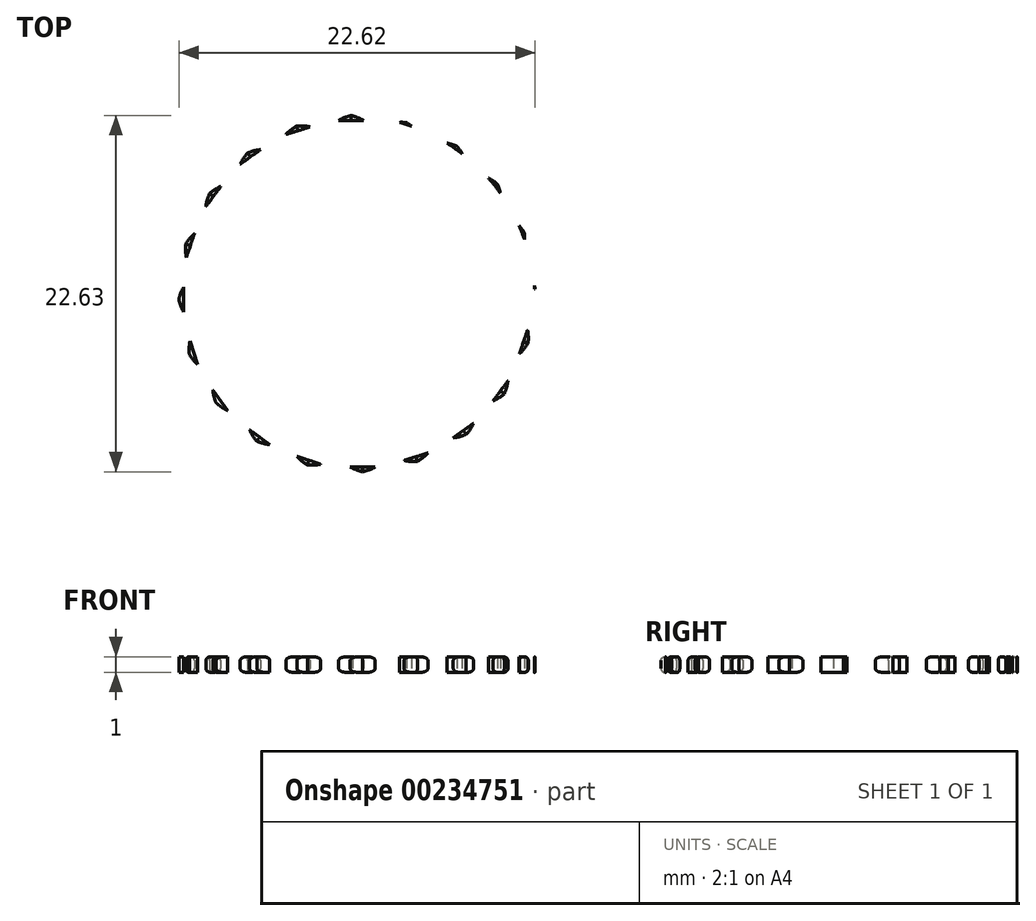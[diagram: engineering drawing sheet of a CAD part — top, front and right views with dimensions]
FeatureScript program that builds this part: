
annotation { "Feature Type Name" : "Feature", "Feature Type Description" : "" }
export const myFeature = defineFeature(function(context is Context, id is Id, definition is map)
    precondition{}
    {
        {
            assignVariable(context, id + "F0", {"name" : "GearDepth", "anyValue" : 1});
        }
        {
            assignVariable(context, id + "F1", {"name" : "TeethFillet", "anyValue" : getVariable(context, 'GearDepth') * .25});
        }
        {
            var Q0;
            Q0=qCreatedBy(makeId("Top.planeOp"),FACE);
            var sketch = newSketch(context, id + "F2", { "sketchPlane" : qUnion([Q0])});
            skCircle(sketch, "E0", {"center": v(0, 0) * mm, "radius": 11.8 * mm});
            skCircle(sketch, "E1", {"center": v(0, 0) * mm, "radius": 11.65 * mm, "construction": true});
            skCircle(sketch, "E2", {"center": v(0, 0) * mm, "radius": 11.5 * mm, "construction": true});
            skLineSegment(sketch, "E3", {"start": v(0, 0) * mm, "end": v(0, 17.6) * mm, "construction": true});
            skLineSegment(sketch, "E4", {"start": v(0, 0) * mm, "end": v(0.18, 18.05) * mm, "construction": true});
            skLineSegment(sketch, "E5", {"start": v(0, 11.65) * mm, "end": v(-10.54, 11.65) * mm, "construction": true});
            skLineSegment(sketch, "E6", {"start": v(0, 11.65) * mm, "end": v(-10.3, 7.9) * mm, "construction": true});
            skCircle(sketch, "E7", {"center": v(0, 11.65) * mm, "radius": 2.91 * mm, "construction": true});
            skCircle(sketch, "E8", {"center": v(-2.74, 10.65) * mm, "radius": 2.91 * mm, "construction": true});
            skArc(sketch, "E9", {"start": v(-5.47, 11.65) * mm, "mid": v(-5.64, 10.86) * mm, "end": v(-5.59, 10.05) * mm});
            skArc(sketch, "E10.trimOffspring", {"start": v(0.2, 11.79) * mm, "mid": v(-0.26, 11.67) * mm, "end": v(-0.68, 11.48) * mm});
            skArc(sketch, "E11.MirrorCS", {"start": v(0.04, 11.8) * mm, "mid": v(0.49, 11.67) * mm, "end": v(0.9, 11.46) * mm});
            skLineSegment(sketch, "E12", {"start": v(-0.68, 11.48) * mm, "end": v(0.9, 11.46) * mm});
            skArc(sketch, "E13.1.0", {"start": v(-3.3, 11.15) * mm, "mid": v(-3.69, 10.9) * mm, "end": v(-4.03, 10.58) * mm});
            skLineSegment(sketch, "E13.1.1", {"start": v(-4.03, 10.58) * mm, "end": v(-2.51, 11.06) * mm});
            skArc(sketch, "E13.1.2", {"start": v(-3.44, 11.1) * mm, "mid": v(-2.97, 11.12) * mm, "end": v(-2.51, 11.06) * mm});
            skArc(sketch, "E13.2.0", {"start": v(-6.4, 9.46) * mm, "mid": v(-6.7, 9.1) * mm, "end": v(-6.93, 8.7) * mm});
            skLineSegment(sketch, "E13.2.1", {"start": v(-6.93, 8.7) * mm, "end": v(-5.64, 9.62) * mm});
            skArc(sketch, "E13.2.2", {"start": v(-6.53, 9.37) * mm, "mid": v(-6.1, 9.53) * mm, "end": v(-5.64, 9.62) * mm});
            skArc(sketch, "E13.3.0", {"start": v(-8.85, 6.9) * mm, "mid": v(-9.02, 6.46) * mm, "end": v(-9.11, 6) * mm});
            skLineSegment(sketch, "E13.3.1", {"start": v(-9.11, 6) * mm, "end": v(-8.17, 7.28) * mm});
            skArc(sketch, "E13.3.2", {"start": v(-8.94, 6.77) * mm, "mid": v(-8.58, 7.06) * mm, "end": v(-8.17, 7.28) * mm});
            skArc(sketch, "E13.4.0", {"start": v(-10.38, 3.7) * mm, "mid": v(-10.4, 3.23) * mm, "end": v(-10.35, 2.77) * mm});
            skLineSegment(sketch, "E13.4.1", {"start": v(-10.35, 2.77) * mm, "end": v(-9.85, 4.27) * mm});
            skArc(sketch, "E13.4.2", {"start": v(-10.43, 3.55) * mm, "mid": v(-10.17, 3.94) * mm, "end": v(-9.85, 4.27) * mm});
            skArc(sketch, "E13.5.0", {"start": v(-10.85, 0.18) * mm, "mid": v(-10.73, -0.27) * mm, "end": v(-10.54, -0.7) * mm});
            skLineSegment(sketch, "E13.5.1", {"start": v(-10.54, -0.7) * mm, "end": v(-10.52, 0.9) * mm});
            skArc(sketch, "E13.5.2", {"start": v(-10.85, 0.03) * mm, "mid": v(-10.72, 0.48) * mm, "end": v(-10.52, 0.9) * mm});
            skArc(sketch, "E13.6.0", {"start": v(-10.2, -3.3) * mm, "mid": v(-9.95, -3.7) * mm, "end": v(-9.64, -4.04) * mm});
            skLineSegment(sketch, "E13.6.1", {"start": v(-9.64, -4.04) * mm, "end": v(-10.11, -2.52) * mm});
            skArc(sketch, "E13.6.2", {"start": v(-10.16, -3.45) * mm, "mid": v(-10.18, -2.98) * mm, "end": v(-10.11, -2.52) * mm});
            skArc(sketch, "E13.7.0", {"start": v(-8.52, -6.42) * mm, "mid": v(-8.16, -6.71) * mm, "end": v(-7.75, -6.94) * mm});
            skLineSegment(sketch, "E13.7.1", {"start": v(-7.75, -6.94) * mm, "end": v(-8.67, -5.65) * mm});
            skArc(sketch, "E13.7.2", {"start": v(-8.43, -6.54) * mm, "mid": v(-8.59, -6.1) * mm, "end": v(-8.67, -5.65) * mm});
            skArc(sketch, "E13.8.0", {"start": v(-5.95, -8.86) * mm, "mid": v(-5.52, -9.03) * mm, "end": v(-5.06, -9.12) * mm});
            skLineSegment(sketch, "E13.8.1", {"start": v(-5.06, -9.12) * mm, "end": v(-6.34, -8.18) * mm});
            skArc(sketch, "E13.8.2", {"start": v(-5.83, -8.95) * mm, "mid": v(-6.11, -8.59) * mm, "end": v(-6.34, -8.18) * mm});
            skArc(sketch, "E13.9.0", {"start": v(-2.75, -10.39) * mm, "mid": v(-2.29, -10.42) * mm, "end": v(-1.82, -10.36) * mm});
            skLineSegment(sketch, "E13.9.1", {"start": v(-1.82, -10.36) * mm, "end": v(-3.33, -9.86) * mm});
            skArc(sketch, "E13.9.2", {"start": v(-2.6, -10.44) * mm, "mid": v(-3, -10.18) * mm, "end": v(-3.33, -9.86) * mm});
            skArc(sketch, "E13.10.0", {"start": v(0.76, -10.85) * mm, "mid": v(1.21, -10.74) * mm, "end": v(1.64, -10.54) * mm});
            skLineSegment(sketch, "E13.10.1", {"start": v(1.64, -10.54) * mm, "end": v(0.05, -10.53) * mm});
            skArc(sketch, "E13.10.2", {"start": v(0.91, -10.86) * mm, "mid": v(0.47, -10.73) * mm, "end": v(0.05, -10.53) * mm});
            skArc(sketch, "E13.11.0", {"start": v(4.25, -10.21) * mm, "mid": v(4.64, -9.96) * mm, "end": v(4.98, -9.65) * mm});
            skLineSegment(sketch, "E13.11.1", {"start": v(4.98, -9.65) * mm, "end": v(3.47, -10.12) * mm});
            skArc(sketch, "E13.11.2", {"start": v(4.4, -10.17) * mm, "mid": v(3.93, -10.19) * mm, "end": v(3.47, -10.12) * mm});
            skArc(sketch, "E13.12.0", {"start": v(7.36, -8.52) * mm, "mid": v(7.66, -8.17) * mm, "end": v(7.89, -7.76) * mm});
            skLineSegment(sketch, "E13.12.1", {"start": v(7.89, -7.76) * mm, "end": v(6.6, -8.68) * mm});
            skArc(sketch, "E13.12.2", {"start": v(7.49, -8.44) * mm, "mid": v(7.05, -8.6) * mm, "end": v(6.6, -8.68) * mm});
            skArc(sketch, "E13.13.0", {"start": v(9.8, -5.96) * mm, "mid": v(9.98, -5.52) * mm, "end": v(10.07, -5.07) * mm});
            skLineSegment(sketch, "E13.13.1", {"start": v(10.07, -5.07) * mm, "end": v(9.12, -6.34) * mm});
            skArc(sketch, "E13.13.2", {"start": v(9.9, -5.83) * mm, "mid": v(9.53, -6.12) * mm, "end": v(9.12, -6.34) * mm});
            skArc(sketch, "E13.14.0", {"start": v(11.33, -2.76) * mm, "mid": v(11.36, -2.3) * mm, "end": v(11.3, -1.83) * mm});
            skLineSegment(sketch, "E13.14.1", {"start": v(11.3, -1.83) * mm, "end": v(10.8, -3.34) * mm});
            skArc(sketch, "E13.14.2", {"start": v(11.38, -2.62) * mm, "mid": v(11.12, -3) * mm, "end": v(10.8, -3.34) * mm});
            skArc(sketch, "E13.15.0", {"start": v(11.8, 0.75) * mm, "mid": v(11.68, 1.2) * mm, "end": v(11.49, 1.63) * mm});
            skLineSegment(sketch, "E13.15.1", {"start": v(11.49, 1.63) * mm, "end": v(11.47, 0.04) * mm});
            skArc(sketch, "E13.15.2", {"start": v(11.8, 0.9) * mm, "mid": v(11.68, 0.46) * mm, "end": v(11.47, 0.04) * mm});
            skArc(sketch, "E13.16.0", {"start": v(11.16, 4.24) * mm, "mid": v(10.9, 4.63) * mm, "end": v(10.6, 4.97) * mm});
            skLineSegment(sketch, "E13.16.1", {"start": v(10.6, 4.97) * mm, "end": v(11.07, 3.46) * mm});
            skArc(sketch, "E13.16.2", {"start": v(11.11, 4.38) * mm, "mid": v(11.13, 3.92) * mm, "end": v(11.07, 3.46) * mm});
            skArc(sketch, "E13.17.0", {"start": v(9.47, 7.35) * mm, "mid": v(9.11, 7.65) * mm, "end": v(8.7, 7.88) * mm});
            skLineSegment(sketch, "E13.17.1", {"start": v(8.7, 7.88) * mm, "end": v(9.63, 6.58) * mm});
            skArc(sketch, "E13.17.2", {"start": v(9.38, 7.48) * mm, "mid": v(9.54, 7.04) * mm, "end": v(9.63, 6.58) * mm});
            skArc(sketch, "E13.18.0", {"start": v(6.9, 9.8) * mm, "mid": v(6.47, 9.97) * mm, "end": v(6.01, 10.06) * mm});
            skLineSegment(sketch, "E13.18.1", {"start": v(6.01, 10.06) * mm, "end": v(7.29, 9.11) * mm});
            skArc(sketch, "E13.18.2", {"start": v(6.78, 9.89) * mm, "mid": v(7.07, 9.52) * mm, "end": v(7.29, 9.11) * mm});
            skArc(sketch, "E13.19.0", {"start": v(3.7, 11.32) * mm, "mid": v(3.24, 11.35) * mm, "end": v(2.78, 11.3) * mm});
            skLineSegment(sketch, "E13.19.1", {"start": v(2.78, 11.3) * mm, "end": v(4.28, 10.8) * mm});
            skArc(sketch, "E13.19.2", {"start": v(3.56, 11.37) * mm, "mid": v(3.95, 11.11) * mm, "end": v(4.28, 10.8) * mm});
            skPoint(sketch, "E13.center", {"position": v(0.48, 0.47) * mm});
            skCircle(sketch, "E14", {"center": v(0, 0) * mm, "radius": 2.5 * mm});
            skSolve(sketch);
        }
        {
            var Q0;
            {var subQ0=sQuery(id+"F2.wireOp",EDGE,"E10.trimOffspring");Q0=makeQuery(id+"F2.imprint","IMPRINT",FACE,{"disambiguationData":[TD([[makeQuery(id+"F2.imprint","IMPRINT",EDGE,{"derivedFrom":subQ0}),1.0]])]});}
            var Q1;
            {var subQ0=sQuery(id+"F2.wireOp",EDGE,"E0");var subQ1=makeQuery(id+"F2.imprint","INTERSECT",VERTEX,{"derivedFrom":[subQ0,sQuery(id+"F2.wireOp",EDGE,"E10.trimOffspring")]});Q1=makeQuery(id+"F2.imprint","IMPRINT",FACE,{"disambiguationData":[TD([[makeQuery(id+"F2.imprint","IMPRINT",EDGE,{"disambiguationData":[TD([[subQ1,-1.0]])],"derivedFrom":subQ0}),1.0]])]});}
            var Q2;
            {var subQ0=sQuery(id+"F2.wireOp",EDGE,"E13.1.0");Q2=makeQuery(id+"F2.imprint","IMPRINT",FACE,{"disambiguationData":[TD([[makeQuery(id+"F2.imprint","IMPRINT",EDGE,{"derivedFrom":subQ0}),1.0]])]});}
            var Q3;
            {var subQ0=sQuery(id+"F2.wireOp",EDGE,"E13.2.0");Q3=makeQuery(id+"F2.imprint","IMPRINT",FACE,{"disambiguationData":[TD([[makeQuery(id+"F2.imprint","IMPRINT",EDGE,{"derivedFrom":subQ0}),1.0]])]});}
            var Q4;
            {var subQ0=sQuery(id+"F2.wireOp",EDGE,"E13.3.0");Q4=makeQuery(id+"F2.imprint","IMPRINT",FACE,{"disambiguationData":[TD([[makeQuery(id+"F2.imprint","IMPRINT",EDGE,{"derivedFrom":subQ0}),1.0]])]});}
            var Q5;
            {var subQ0=sQuery(id+"F2.wireOp",EDGE,"E13.4.0");Q5=makeQuery(id+"F2.imprint","IMPRINT",FACE,{"disambiguationData":[TD([[makeQuery(id+"F2.imprint","IMPRINT",EDGE,{"derivedFrom":subQ0}),1.0]])]});}
            var Q6;
            {var subQ0=sQuery(id+"F2.wireOp",EDGE,"E13.5.0");Q6=makeQuery(id+"F2.imprint","IMPRINT",FACE,{"disambiguationData":[TD([[makeQuery(id+"F2.imprint","IMPRINT",EDGE,{"derivedFrom":subQ0}),1.0]])]});}
            var Q7;
            {var subQ0=sQuery(id+"F2.wireOp",EDGE,"E13.6.0");Q7=makeQuery(id+"F2.imprint","IMPRINT",FACE,{"disambiguationData":[TD([[makeQuery(id+"F2.imprint","IMPRINT",EDGE,{"derivedFrom":subQ0}),1.0]])]});}
            var Q8;
            {var subQ0=sQuery(id+"F2.wireOp",EDGE,"E13.7.0");Q8=makeQuery(id+"F2.imprint","IMPRINT",FACE,{"disambiguationData":[TD([[makeQuery(id+"F2.imprint","IMPRINT",EDGE,{"derivedFrom":subQ0}),1.0]])]});}
            var Q9;
            {var subQ0=sQuery(id+"F2.wireOp",EDGE,"E13.8.0");Q9=makeQuery(id+"F2.imprint","IMPRINT",FACE,{"disambiguationData":[TD([[makeQuery(id+"F2.imprint","IMPRINT",EDGE,{"derivedFrom":subQ0}),1.0]])]});}
            var Q10;
            {var subQ0=sQuery(id+"F2.wireOp",EDGE,"E13.9.0");Q10=makeQuery(id+"F2.imprint","IMPRINT",FACE,{"disambiguationData":[TD([[makeQuery(id+"F2.imprint","IMPRINT",EDGE,{"derivedFrom":subQ0}),1.0]])]});}
            var Q11;
            {var subQ0=sQuery(id+"F2.wireOp",EDGE,"E13.10.0");Q11=makeQuery(id+"F2.imprint","IMPRINT",FACE,{"disambiguationData":[TD([[makeQuery(id+"F2.imprint","IMPRINT",EDGE,{"derivedFrom":subQ0}),1.0]])]});}
            var Q12;
            {var subQ0=sQuery(id+"F2.wireOp",EDGE,"E13.11.0");Q12=makeQuery(id+"F2.imprint","IMPRINT",FACE,{"disambiguationData":[TD([[makeQuery(id+"F2.imprint","IMPRINT",EDGE,{"derivedFrom":subQ0}),1.0]])]});}
            var Q13;
            {var subQ0=sQuery(id+"F2.wireOp",EDGE,"E13.12.0");Q13=makeQuery(id+"F2.imprint","IMPRINT",FACE,{"disambiguationData":[TD([[makeQuery(id+"F2.imprint","IMPRINT",EDGE,{"derivedFrom":subQ0}),1.0]])]});}
            var Q14;
            {var subQ0=sQuery(id+"F2.wireOp",EDGE,"E13.13.0");Q14=makeQuery(id+"F2.imprint","IMPRINT",FACE,{"disambiguationData":[TD([[makeQuery(id+"F2.imprint","IMPRINT",EDGE,{"derivedFrom":subQ0}),1.0]])]});}
            var Q15;
            {var subQ0=sQuery(id+"F2.wireOp",EDGE,"E13.14.0");Q15=makeQuery(id+"F2.imprint","IMPRINT",FACE,{"disambiguationData":[TD([[makeQuery(id+"F2.imprint","IMPRINT",EDGE,{"derivedFrom":subQ0}),1.0]])]});}
            var Q16;
            {var subQ0=sQuery(id+"F2.wireOp",EDGE,"E13.15.0");Q16=makeQuery(id+"F2.imprint","IMPRINT",FACE,{"disambiguationData":[TD([[makeQuery(id+"F2.imprint","IMPRINT",EDGE,{"derivedFrom":subQ0}),1.0]])]});}
            var Q17;
            {var subQ0=sQuery(id+"F2.wireOp",EDGE,"E13.16.0");Q17=makeQuery(id+"F2.imprint","IMPRINT",FACE,{"disambiguationData":[TD([[makeQuery(id+"F2.imprint","IMPRINT",EDGE,{"derivedFrom":subQ0}),1.0]])]});}
            var Q18;
            {var subQ0=sQuery(id+"F2.wireOp",EDGE,"E13.17.0");Q18=makeQuery(id+"F2.imprint","IMPRINT",FACE,{"disambiguationData":[TD([[makeQuery(id+"F2.imprint","IMPRINT",EDGE,{"derivedFrom":subQ0}),1.0]])]});}
            var Q19;
            {var subQ0=sQuery(id+"F2.wireOp",EDGE,"E13.18.0");Q19=makeQuery(id+"F2.imprint","IMPRINT",FACE,{"disambiguationData":[TD([[makeQuery(id+"F2.imprint","IMPRINT",EDGE,{"derivedFrom":subQ0}),1.0]])]});}
            var Q20;
            {var subQ0=sQuery(id+"F2.wireOp",EDGE,"E13.19.0");Q20=makeQuery(id+"F2.imprint","IMPRINT",FACE,{"disambiguationData":[TD([[makeQuery(id+"F2.imprint","IMPRINT",EDGE,{"derivedFrom":subQ0}),1.0]])]});}
            var Q21;
            Q21=sQuery(id+"F2.wireOp",EDGE,"E0");
            var Q22;
            Q22=sQuery(id+"F2.wireOp",EDGE,"E10.trimOffspring");
            var Q23;
            Q23=sQuery(id+"F2.wireOp",EDGE,"E12");
            var Q24;
            Q24=sQuery(id+"F2.wireOp",EDGE,"E11.MirrorCS");
            extrude(context, id + "F3", {"entities" : qUnion([Q0, Q1, Q2, Q3, Q4, Q5, Q6, Q7, Q8, Q9, Q10, Q11, Q12, Q13, Q14, Q15, Q16, Q17, Q18, Q19, Q20]), "surfaceEntities" : qUnion([Q21, Q22, Q23, Q24]), "depth" : (getVariable(context, 'GearDepth')) * mm});
        }
        {
            var Q0;
            Q0=makeQuery(id+"F3.opExtrude","CAP_EDGE",EDGE,{"disambiguationData":[OSD([sQuery(id+"F2.wireOp",EDGE,"E13.5.2")])],"isStart":false});
            var Q1;
            Q1=makeQuery(id+"F3.opExtrude","CAP_EDGE",EDGE,{"disambiguationData":[OSD([sQuery(id+"F2.wireOp",EDGE,"E13.5.1")])],"isStart":false});
            var Q2;
            {var subQ0=sQuery(id+"F2.wireOp",EDGE,"E0");Q2=makeQuery(id+"F3.opExtrude","CAP_EDGE",EDGE,{"disambiguationData":[OSD([subQ0]),TDD([makeQuery(id+"F2.imprint","IMPRINT",EDGE,{"disambiguationData":[TD([[makeQuery(id+"F2.imprint","INTERSECT",VERTEX,{"derivedFrom":[subQ0,sQuery(id+"F2.wireOp",EDGE,"E13.5.2")]}),-1.0]])],"derivedFrom":subQ0})])],"isStart":false});}
            var Q3;
            Q3=makeQuery(id+"F3.opExtrude","CAP_EDGE",EDGE,{"disambiguationData":[OSD([sQuery(id+"F2.wireOp",EDGE,"E13.6.0")])],"isStart":false});
            var Q4;
            Q4=makeQuery(id+"F3.opExtrude","CAP_EDGE",EDGE,{"disambiguationData":[OSD([sQuery(id+"F2.wireOp",EDGE,"E13.6.1")])],"isStart":false});
            var Q5;
            Q5=makeQuery(id+"F3.opExtrude","CAP_EDGE",EDGE,{"disambiguationData":[OSD([sQuery(id+"F2.wireOp",EDGE,"E13.6.2")])],"isStart":false});
            var Q6;
            {var subQ0=sQuery(id+"F2.wireOp",EDGE,"E0");Q6=makeQuery(id+"F3.opExtrude","SWEPT_FACE",FACE,{"disambiguationData":[OSD([subQ0]),TDD([makeQuery(id+"F2.imprint","IMPRINT",EDGE,{"disambiguationData":[TD([[makeQuery(id+"F2.imprint","INTERSECT",VERTEX,{"derivedFrom":[subQ0,sQuery(id+"F2.wireOp",EDGE,"E13.6.2")]}),-1.0]])],"derivedFrom":subQ0})])]});}
            var Q7;
            {var subQ0=sQuery(id+"F2.wireOp",EDGE,"E0");Q7=makeQuery(id+"F3.opExtrude","CAP_EDGE",EDGE,{"disambiguationData":[OSD([subQ0]),TDD([makeQuery(id+"F2.imprint","IMPRINT",EDGE,{"disambiguationData":[TD([[makeQuery(id+"F2.imprint","INTERSECT",VERTEX,{"derivedFrom":[subQ0,sQuery(id+"F2.wireOp",EDGE,"E13.6.2")]}),-1.0]])],"derivedFrom":subQ0})])],"isStart":false});}
            var Q8;
            Q8=makeQuery(id+"F3.opExtrude","CAP_EDGE",EDGE,{"disambiguationData":[OSD([sQuery(id+"F2.wireOp",EDGE,"E13.7.2")])],"isStart":true});
            var Q9;
            {var subQ0=sQuery(id+"F2.wireOp",EDGE,"E0");Q9=makeQuery(id+"F3.opExtrude","CAP_EDGE",EDGE,{"disambiguationData":[OSD([subQ0]),TDD([makeQuery(id+"F2.imprint","IMPRINT",EDGE,{"disambiguationData":[TD([[makeQuery(id+"F2.imprint","INTERSECT",VERTEX,{"derivedFrom":[subQ0,sQuery(id+"F2.wireOp",EDGE,"E13.7.2")]}),-1.0]])],"derivedFrom":subQ0})])],"isStart":true});}
            var Q10;
            Q10=makeQuery(id+"F3.opExtrude","CAP_EDGE",EDGE,{"disambiguationData":[OSD([sQuery(id+"F2.wireOp",EDGE,"E13.7.2")])],"isStart":false});
            var Q11;
            {var subQ0=sQuery(id+"F2.wireOp",EDGE,"E0");Q11=makeQuery(id+"F3.opExtrude","CAP_EDGE",EDGE,{"disambiguationData":[OSD([subQ0]),TDD([makeQuery(id+"F2.imprint","IMPRINT",EDGE,{"disambiguationData":[TD([[makeQuery(id+"F2.imprint","INTERSECT",VERTEX,{"derivedFrom":[subQ0,sQuery(id+"F2.wireOp",EDGE,"E13.7.2")]}),-1.0]])],"derivedFrom":subQ0})])],"isStart":false});}
            var Q12;
            Q12=makeQuery(id+"F3.opExtrude","CAP_EDGE",EDGE,{"disambiguationData":[OSD([sQuery(id+"F2.wireOp",EDGE,"E13.8.0")])],"isStart":false});
            var Q13;
            {var subQ0=sQuery(id+"F2.wireOp",EDGE,"E0");Q13=makeQuery(id+"F3.opExtrude","SWEPT_FACE",FACE,{"disambiguationData":[OSD([subQ0]),TDD([makeQuery(id+"F2.imprint","IMPRINT",EDGE,{"disambiguationData":[TD([[makeQuery(id+"F2.imprint","INTERSECT",VERTEX,{"derivedFrom":[subQ0,sQuery(id+"F2.wireOp",EDGE,"E13.7.2")]}),-1.0]])],"derivedFrom":subQ0})])]});}
            var Q14;
            Q14=makeQuery(id+"F3.opExtrude","CAP_EDGE",EDGE,{"disambiguationData":[OSD([sQuery(id+"F2.wireOp",EDGE,"E13.6.0")])],"isStart":true});
            var Q15;
            Q15=makeQuery(id+"F3.opExtrude","CAP_EDGE",EDGE,{"disambiguationData":[OSD([sQuery(id+"F2.wireOp",EDGE,"E13.8.2")])],"isStart":false});
            var Q16;
            {var subQ0=sQuery(id+"F2.wireOp",EDGE,"E0");Q16=makeQuery(id+"F3.opExtrude","CAP_EDGE",EDGE,{"disambiguationData":[OSD([subQ0]),TDD([makeQuery(id+"F2.imprint","IMPRINT",EDGE,{"disambiguationData":[TD([[makeQuery(id+"F2.imprint","INTERSECT",VERTEX,{"derivedFrom":[subQ0,sQuery(id+"F2.wireOp",EDGE,"E13.8.2")]}),-1.0]])],"derivedFrom":subQ0})])],"isStart":false});}
            var Q17;
            Q17=makeQuery(id+"F3.opExtrude","CAP_EDGE",EDGE,{"disambiguationData":[OSD([sQuery(id+"F2.wireOp",EDGE,"E13.9.0")])],"isStart":false});
            var Q18;
            Q18=makeQuery(id+"F3.opExtrude","CAP_EDGE",EDGE,{"disambiguationData":[OSD([sQuery(id+"F2.wireOp",EDGE,"E13.9.2")])],"isStart":false});
            var Q19;
            {var subQ0=sQuery(id+"F2.wireOp",EDGE,"E0");Q19=makeQuery(id+"F3.opExtrude","CAP_EDGE",EDGE,{"disambiguationData":[OSD([subQ0]),TDD([makeQuery(id+"F2.imprint","IMPRINT",EDGE,{"disambiguationData":[TD([[makeQuery(id+"F2.imprint","INTERSECT",VERTEX,{"derivedFrom":[subQ0,sQuery(id+"F2.wireOp",EDGE,"E13.9.2")]}),-1.0]])],"derivedFrom":subQ0})])],"isStart":false});}
            var Q20;
            Q20=makeQuery(id+"F3.opExtrude","CAP_EDGE",EDGE,{"disambiguationData":[OSD([sQuery(id+"F2.wireOp",EDGE,"E13.10.0")])],"isStart":false});
            var Q21;
            Q21=makeQuery(id+"F3.opExtrude","CAP_EDGE",EDGE,{"disambiguationData":[OSD([sQuery(id+"F2.wireOp",EDGE,"E13.10.2")])],"isStart":false});
            var Q22;
            {var subQ0=sQuery(id+"F2.wireOp",EDGE,"E0");Q22=makeQuery(id+"F3.opExtrude","CAP_EDGE",EDGE,{"disambiguationData":[OSD([subQ0]),TDD([makeQuery(id+"F2.imprint","IMPRINT",EDGE,{"disambiguationData":[TD([[makeQuery(id+"F2.imprint","INTERSECT",VERTEX,{"derivedFrom":[subQ0,sQuery(id+"F2.wireOp",EDGE,"E13.10.2")]}),-1.0]])],"derivedFrom":subQ0})])],"isStart":false});}
            var Q23;
            Q23=makeQuery(id+"F3.opExtrude","CAP_EDGE",EDGE,{"disambiguationData":[OSD([sQuery(id+"F2.wireOp",EDGE,"E13.11.0")])],"isStart":false});
            var Q24;
            Q24=makeQuery(id+"F3.opExtrude","CAP_EDGE",EDGE,{"disambiguationData":[OSD([sQuery(id+"F2.wireOp",EDGE,"E13.11.2")])],"isStart":false});
            var Q25;
            {var subQ0=sQuery(id+"F2.wireOp",EDGE,"E0");Q25=makeQuery(id+"F3.opExtrude","CAP_EDGE",EDGE,{"disambiguationData":[OSD([subQ0]),TDD([makeQuery(id+"F2.imprint","IMPRINT",EDGE,{"disambiguationData":[TD([[makeQuery(id+"F2.imprint","INTERSECT",VERTEX,{"derivedFrom":[subQ0,sQuery(id+"F2.wireOp",EDGE,"E13.11.2")]}),-1.0]])],"derivedFrom":subQ0})])],"isStart":false});}
            var Q26;
            Q26=makeQuery(id+"F3.opExtrude","CAP_EDGE",EDGE,{"disambiguationData":[OSD([sQuery(id+"F2.wireOp",EDGE,"E13.12.0")])],"isStart":false});
            var Q27;
            Q27=makeQuery(id+"F3.opExtrude","CAP_EDGE",EDGE,{"disambiguationData":[OSD([sQuery(id+"F2.wireOp",EDGE,"E13.12.2")])],"isStart":false});
            var Q28;
            {var subQ0=sQuery(id+"F2.wireOp",EDGE,"E0");Q28=makeQuery(id+"F3.opExtrude","CAP_EDGE",EDGE,{"disambiguationData":[OSD([subQ0]),TDD([makeQuery(id+"F2.imprint","IMPRINT",EDGE,{"disambiguationData":[TD([[makeQuery(id+"F2.imprint","INTERSECT",VERTEX,{"derivedFrom":[subQ0,sQuery(id+"F2.wireOp",EDGE,"E13.12.2")]}),-1.0]])],"derivedFrom":subQ0})])],"isStart":false});}
            var Q29;
            Q29=makeQuery(id+"F3.opExtrude","CAP_EDGE",EDGE,{"disambiguationData":[OSD([sQuery(id+"F2.wireOp",EDGE,"E13.13.0")])],"isStart":false});
            var Q30;
            Q30=makeQuery(id+"F3.opExtrude","CAP_EDGE",EDGE,{"disambiguationData":[OSD([sQuery(id+"F2.wireOp",EDGE,"E13.13.2")])],"isStart":false});
            var Q31;
            {var subQ0=sQuery(id+"F2.wireOp",EDGE,"E0");Q31=makeQuery(id+"F3.opExtrude","CAP_EDGE",EDGE,{"disambiguationData":[OSD([subQ0]),TDD([makeQuery(id+"F2.imprint","IMPRINT",EDGE,{"disambiguationData":[TD([[makeQuery(id+"F2.imprint","INTERSECT",VERTEX,{"derivedFrom":[subQ0,sQuery(id+"F2.wireOp",EDGE,"E13.13.2")]}),-1.0]])],"derivedFrom":subQ0})])],"isStart":false});}
            var Q32;
            Q32=makeQuery(id+"F3.opExtrude","CAP_EDGE",EDGE,{"disambiguationData":[OSD([sQuery(id+"F2.wireOp",EDGE,"E13.14.0")])],"isStart":false});
            var Q33;
            Q33=makeQuery(id+"F3.opExtrude","CAP_EDGE",EDGE,{"disambiguationData":[OSD([sQuery(id+"F2.wireOp",EDGE,"E13.14.2")])],"isStart":false});
            var Q34;
            {var subQ0=sQuery(id+"F2.wireOp",EDGE,"E0");Q34=makeQuery(id+"F3.opExtrude","CAP_EDGE",EDGE,{"disambiguationData":[OSD([subQ0]),TDD([makeQuery(id+"F2.imprint","IMPRINT",EDGE,{"disambiguationData":[TD([[makeQuery(id+"F2.imprint","INTERSECT",VERTEX,{"derivedFrom":[subQ0,sQuery(id+"F2.wireOp",EDGE,"E13.14.2")]}),-1.0]])],"derivedFrom":subQ0})])],"isStart":false});}
            var Q35;
            Q35=makeQuery(id+"F3.opExtrude","CAP_EDGE",EDGE,{"disambiguationData":[OSD([sQuery(id+"F2.wireOp",EDGE,"E13.15.0")])],"isStart":false});
            var Q36;
            {var subQ0=sQuery(id+"F2.wireOp",EDGE,"E0");Q36=makeQuery(id+"F3.opExtrude","CAP_EDGE",EDGE,{"disambiguationData":[OSD([subQ0]),TDD([makeQuery(id+"F2.imprint","IMPRINT",EDGE,{"disambiguationData":[TD([[makeQuery(id+"F2.imprint","INTERSECT",VERTEX,{"derivedFrom":[subQ0,sQuery(id+"F2.wireOp",EDGE,"E13.14.2")]}),-1.0]])],"derivedFrom":subQ0})])],"isStart":false});}
            var Q37;
            Q37=makeQuery(id+"F3.opExtrude","CAP_EDGE",EDGE,{"disambiguationData":[OSD([sQuery(id+"F2.wireOp",EDGE,"E13.15.2")])],"isStart":false});
            var Q38;
            {var subQ0=sQuery(id+"F2.wireOp",EDGE,"E0");Q38=makeQuery(id+"F3.opExtrude","CAP_EDGE",EDGE,{"disambiguationData":[OSD([subQ0]),TDD([makeQuery(id+"F2.imprint","IMPRINT",EDGE,{"disambiguationData":[TD([[makeQuery(id+"F2.imprint","INTERSECT",VERTEX,{"derivedFrom":[subQ0,sQuery(id+"F2.wireOp",EDGE,"E13.15.2")]}),-1.0]])],"derivedFrom":subQ0})])],"isStart":false});}
            var Q39;
            Q39=makeQuery(id+"F3.opExtrude","CAP_EDGE",EDGE,{"disambiguationData":[OSD([sQuery(id+"F2.wireOp",EDGE,"E13.16.0")])],"isStart":false});
            var Q40;
            Q40=makeQuery(id+"F3.opExtrude","CAP_EDGE",EDGE,{"disambiguationData":[OSD([sQuery(id+"F2.wireOp",EDGE,"E13.16.2")])],"isStart":false});
            var Q41;
            Q41=makeQuery(id+"F3.opExtrude","CAP_EDGE",EDGE,{"disambiguationData":[OSD([sQuery(id+"F2.wireOp",EDGE,"E13.17.0")])],"isStart":false});
            var Q42;
            {var subQ0=sQuery(id+"F2.wireOp",EDGE,"E0");Q42=makeQuery(id+"F3.opExtrude","CAP_EDGE",EDGE,{"disambiguationData":[OSD([subQ0]),TDD([makeQuery(id+"F2.imprint","IMPRINT",EDGE,{"disambiguationData":[TD([[makeQuery(id+"F2.imprint","INTERSECT",VERTEX,{"derivedFrom":[subQ0,sQuery(id+"F2.wireOp",EDGE,"E13.16.2")]}),-1.0]])],"derivedFrom":subQ0})])],"isStart":false});}
            var Q43;
            Q43=makeQuery(id+"F3.opExtrude","CAP_EDGE",EDGE,{"disambiguationData":[OSD([sQuery(id+"F2.wireOp",EDGE,"E13.17.2")])],"isStart":false});
            var Q44;
            {var subQ0=sQuery(id+"F2.wireOp",EDGE,"E0");Q44=makeQuery(id+"F3.opExtrude","CAP_EDGE",EDGE,{"disambiguationData":[OSD([subQ0]),TDD([makeQuery(id+"F2.imprint","IMPRINT",EDGE,{"disambiguationData":[TD([[makeQuery(id+"F2.imprint","INTERSECT",VERTEX,{"derivedFrom":[subQ0,sQuery(id+"F2.wireOp",EDGE,"E13.17.2")]}),-1.0]])],"derivedFrom":subQ0})])],"isStart":false});}
            var Q45;
            Q45=makeQuery(id+"F3.opExtrude","CAP_EDGE",EDGE,{"disambiguationData":[OSD([sQuery(id+"F2.wireOp",EDGE,"E13.18.0")])],"isStart":false});
            var Q46;
            Q46=makeQuery(id+"F3.opExtrude","CAP_EDGE",EDGE,{"disambiguationData":[OSD([sQuery(id+"F2.wireOp",EDGE,"E13.18.2")])],"isStart":false});
            var Q47;
            {var subQ0=sQuery(id+"F2.wireOp",EDGE,"E0");Q47=makeQuery(id+"F3.opExtrude","CAP_EDGE",EDGE,{"disambiguationData":[OSD([subQ0]),TDD([makeQuery(id+"F2.imprint","IMPRINT",EDGE,{"disambiguationData":[TD([[makeQuery(id+"F2.imprint","INTERSECT",VERTEX,{"derivedFrom":[subQ0,sQuery(id+"F2.wireOp",EDGE,"E13.18.2")]}),-1.0]])],"derivedFrom":subQ0})])],"isStart":false});}
            var Q48;
            Q48=makeQuery(id+"F3.opExtrude","CAP_EDGE",EDGE,{"disambiguationData":[OSD([sQuery(id+"F2.wireOp",EDGE,"E13.19.0")])],"isStart":false});
            var Q49;
            Q49=makeQuery(id+"F3.opExtrude","CAP_EDGE",EDGE,{"disambiguationData":[OSD([sQuery(id+"F2.wireOp",EDGE,"E13.19.2")])],"isStart":false});
            var Q50;
            Q50=makeQuery(id+"F3.opExtrude","CAP_EDGE",EDGE,{"disambiguationData":[OSD([sQuery(id+"F2.wireOp",EDGE,"E10.trimOffspring")])],"isStart":false});
            var Q51;
            Q51=makeQuery(id+"F3.opExtrude","CAP_EDGE",EDGE,{"disambiguationData":[OSD([sQuery(id+"F2.wireOp",EDGE,"E11.MirrorCS")])],"isStart":false});
            var Q52;
            {var subQ0=sQuery(id+"F2.wireOp",EDGE,"E0");Q52=makeQuery(id+"F3.opExtrude","CAP_EDGE",EDGE,{"disambiguationData":[OSD([subQ0]),TDD([makeQuery(id+"F2.imprint","IMPRINT",EDGE,{"disambiguationData":[TD([[makeQuery(id+"F2.imprint","INTERSECT",VERTEX,{"derivedFrom":[subQ0,sQuery(id+"F2.wireOp",EDGE,"E11.MirrorCS")]}),-1.0]])],"derivedFrom":subQ0})])],"isStart":false});}
            var Q53;
            Q53=makeQuery(id+"F3.opExtrude","CAP_EDGE",EDGE,{"disambiguationData":[OSD([sQuery(id+"F2.wireOp",EDGE,"E13.1.0")])],"isStart":false});
            var Q54;
            Q54=makeQuery(id+"F3.opExtrude","CAP_EDGE",EDGE,{"disambiguationData":[OSD([sQuery(id+"F2.wireOp",EDGE,"E13.1.2")])],"isStart":false});
            var Q55;
            {var subQ0=sQuery(id+"F2.wireOp",EDGE,"E0");Q55=makeQuery(id+"F3.opExtrude","CAP_EDGE",EDGE,{"disambiguationData":[OSD([subQ0]),TDD([makeQuery(id+"F2.imprint","IMPRINT",EDGE,{"disambiguationData":[TD([[makeQuery(id+"F2.imprint","INTERSECT",VERTEX,{"derivedFrom":[subQ0,sQuery(id+"F2.wireOp",EDGE,"E13.1.2")]}),-1.0]])],"derivedFrom":subQ0})])],"isStart":false});}
            var Q56;
            Q56=makeQuery(id+"F3.opExtrude","CAP_EDGE",EDGE,{"disambiguationData":[OSD([sQuery(id+"F2.wireOp",EDGE,"E13.2.0")])],"isStart":false});
            var Q57;
            Q57=makeQuery(id+"F3.opExtrude","CAP_EDGE",EDGE,{"disambiguationData":[OSD([sQuery(id+"F2.wireOp",EDGE,"E13.2.2")])],"isStart":false});
            var Q58;
            {var subQ0=sQuery(id+"F2.wireOp",EDGE,"E0");Q58=makeQuery(id+"F3.opExtrude","CAP_EDGE",EDGE,{"disambiguationData":[OSD([subQ0]),TDD([makeQuery(id+"F2.imprint","IMPRINT",EDGE,{"disambiguationData":[TD([[makeQuery(id+"F2.imprint","INTERSECT",VERTEX,{"derivedFrom":[subQ0,sQuery(id+"F2.wireOp",EDGE,"E13.2.2")]}),-1.0]])],"derivedFrom":subQ0})])],"isStart":false});}
            var Q59;
            Q59=makeQuery(id+"F3.opExtrude","CAP_EDGE",EDGE,{"disambiguationData":[OSD([sQuery(id+"F2.wireOp",EDGE,"E13.3.0")])],"isStart":false});
            var Q60;
            Q60=makeQuery(id+"F3.opExtrude","CAP_EDGE",EDGE,{"disambiguationData":[OSD([sQuery(id+"F2.wireOp",EDGE,"E13.3.2")])],"isStart":false});
            var Q61;
            {var subQ0=sQuery(id+"F2.wireOp",EDGE,"E0");Q61=makeQuery(id+"F3.opExtrude","CAP_EDGE",EDGE,{"disambiguationData":[OSD([subQ0]),TDD([makeQuery(id+"F2.imprint","IMPRINT",EDGE,{"disambiguationData":[TD([[makeQuery(id+"F2.imprint","INTERSECT",VERTEX,{"derivedFrom":[subQ0,sQuery(id+"F2.wireOp",EDGE,"E13.3.2")]}),-1.0]])],"derivedFrom":subQ0})])],"isStart":false});}
            var Q62;
            Q62=makeQuery(id+"F3.opExtrude","CAP_EDGE",EDGE,{"disambiguationData":[OSD([sQuery(id+"F2.wireOp",EDGE,"E13.4.0")])],"isStart":false});
            var Q63;
            Q63=makeQuery(id+"F3.opExtrude","CAP_EDGE",EDGE,{"disambiguationData":[OSD([sQuery(id+"F2.wireOp",EDGE,"E13.4.2")])],"isStart":false});
            var Q64;
            {var subQ0=sQuery(id+"F2.wireOp",EDGE,"E0");Q64=makeQuery(id+"F3.opExtrude","CAP_EDGE",EDGE,{"disambiguationData":[OSD([subQ0]),TDD([makeQuery(id+"F2.imprint","IMPRINT",EDGE,{"disambiguationData":[TD([[makeQuery(id+"F2.imprint","INTERSECT",VERTEX,{"derivedFrom":[subQ0,sQuery(id+"F2.wireOp",EDGE,"E13.4.2")]}),-1.0]])],"derivedFrom":subQ0})])],"isStart":false});}
            var Q65;
            {var subQ0=sQuery(id+"F2.wireOp",EDGE,"E0");Q65=makeQuery(id+"F3.opExtrude","CAP_EDGE",EDGE,{"disambiguationData":[OSD([subQ0]),TDD([makeQuery(id+"F2.imprint","IMPRINT",EDGE,{"disambiguationData":[TD([[makeQuery(id+"F2.imprint","INTERSECT",VERTEX,{"derivedFrom":[subQ0,sQuery(id+"F2.wireOp",EDGE,"E13.5.2")]}),-1.0]])],"derivedFrom":subQ0})])],"isStart":true});}
            var Q66;
            Q66=makeQuery(id+"F3.opExtrude","CAP_EDGE",EDGE,{"disambiguationData":[OSD([sQuery(id+"F2.wireOp",EDGE,"E13.5.2")])],"isStart":true});
            var Q67;
            {var subQ0=sQuery(id+"F2.wireOp",EDGE,"E0");Q67=makeQuery(id+"F3.opExtrude","CAP_EDGE",EDGE,{"disambiguationData":[OSD([subQ0]),TDD([makeQuery(id+"F2.imprint","IMPRINT",EDGE,{"disambiguationData":[TD([[makeQuery(id+"F2.imprint","INTERSECT",VERTEX,{"derivedFrom":[subQ0,sQuery(id+"F2.wireOp",EDGE,"E13.4.2")]}),-1.0]])],"derivedFrom":subQ0})])],"isStart":true});}
            var Q68;
            Q68=makeQuery(id+"F3.opExtrude","CAP_EDGE",EDGE,{"disambiguationData":[OSD([sQuery(id+"F2.wireOp",EDGE,"E13.4.2")])],"isStart":true});
            var Q69;
            Q69=makeQuery(id+"F3.opExtrude","CAP_EDGE",EDGE,{"disambiguationData":[OSD([sQuery(id+"F2.wireOp",EDGE,"E13.4.0")])],"isStart":true});
            var Q70;
            {var subQ0=sQuery(id+"F2.wireOp",EDGE,"E0");Q70=makeQuery(id+"F3.opExtrude","CAP_EDGE",EDGE,{"disambiguationData":[OSD([subQ0]),TDD([makeQuery(id+"F2.imprint","IMPRINT",EDGE,{"disambiguationData":[TD([[makeQuery(id+"F2.imprint","INTERSECT",VERTEX,{"derivedFrom":[subQ0,sQuery(id+"F2.wireOp",EDGE,"E13.3.2")]}),-1.0]])],"derivedFrom":subQ0})])],"isStart":true});}
            var Q71;
            Q71=makeQuery(id+"F3.opExtrude","CAP_EDGE",EDGE,{"disambiguationData":[OSD([sQuery(id+"F2.wireOp",EDGE,"E13.3.2")])],"isStart":true});
            var Q72;
            Q72=makeQuery(id+"F3.opExtrude","CAP_EDGE",EDGE,{"disambiguationData":[OSD([sQuery(id+"F2.wireOp",EDGE,"E13.3.0")])],"isStart":true});
            var Q73;
            {var subQ0=sQuery(id+"F2.wireOp",EDGE,"E0");Q73=makeQuery(id+"F3.opExtrude","CAP_EDGE",EDGE,{"disambiguationData":[OSD([subQ0]),TDD([makeQuery(id+"F2.imprint","IMPRINT",EDGE,{"disambiguationData":[TD([[makeQuery(id+"F2.imprint","INTERSECT",VERTEX,{"derivedFrom":[subQ0,sQuery(id+"F2.wireOp",EDGE,"E13.2.2")]}),-1.0]])],"derivedFrom":subQ0})])],"isStart":true});}
            var Q74;
            Q74=makeQuery(id+"F3.opExtrude","CAP_EDGE",EDGE,{"disambiguationData":[OSD([sQuery(id+"F2.wireOp",EDGE,"E13.2.2")])],"isStart":true});
            var Q75;
            Q75=makeQuery(id+"F3.opExtrude","CAP_EDGE",EDGE,{"disambiguationData":[OSD([sQuery(id+"F2.wireOp",EDGE,"E13.2.0")])],"isStart":true});
            var Q76;
            Q76=makeQuery(id+"F3.opExtrude","CAP_EDGE",EDGE,{"disambiguationData":[OSD([sQuery(id+"F2.wireOp",EDGE,"E13.1.2")])],"isStart":true});
            var Q77;
            {var subQ0=sQuery(id+"F2.wireOp",EDGE,"E0");Q77=makeQuery(id+"F3.opExtrude","CAP_EDGE",EDGE,{"disambiguationData":[OSD([subQ0]),TDD([makeQuery(id+"F2.imprint","IMPRINT",EDGE,{"disambiguationData":[TD([[makeQuery(id+"F2.imprint","INTERSECT",VERTEX,{"derivedFrom":[subQ0,sQuery(id+"F2.wireOp",EDGE,"E13.1.2")]}),-1.0]])],"derivedFrom":subQ0})])],"isStart":true});}
            var Q78;
            Q78=makeQuery(id+"F3.opExtrude","CAP_EDGE",EDGE,{"disambiguationData":[OSD([sQuery(id+"F2.wireOp",EDGE,"E13.1.0")])],"isStart":true});
            var Q79;
            {var subQ0=sQuery(id+"F2.wireOp",EDGE,"E0");Q79=makeQuery(id+"F3.opExtrude","CAP_EDGE",EDGE,{"disambiguationData":[OSD([subQ0]),TDD([makeQuery(id+"F2.imprint","IMPRINT",EDGE,{"disambiguationData":[TD([[makeQuery(id+"F2.imprint","INTERSECT",VERTEX,{"derivedFrom":[subQ0,sQuery(id+"F2.wireOp",EDGE,"E11.MirrorCS")]}),-1.0]])],"derivedFrom":subQ0})])],"isStart":true});}
            var Q80;
            Q80=makeQuery(id+"F3.opExtrude","CAP_EDGE",EDGE,{"disambiguationData":[OSD([sQuery(id+"F2.wireOp",EDGE,"E11.MirrorCS")])],"isStart":true});
            var Q81;
            Q81=makeQuery(id+"F3.opExtrude","CAP_EDGE",EDGE,{"disambiguationData":[OSD([sQuery(id+"F2.wireOp",EDGE,"E10.trimOffspring")])],"isStart":true});
            var Q82;
            {var subQ0=sQuery(id+"F2.wireOp",EDGE,"E0");Q82=makeQuery(id+"F3.opExtrude","CAP_EDGE",EDGE,{"disambiguationData":[OSD([subQ0]),TDD([makeQuery(id+"F2.imprint","IMPRINT",EDGE,{"disambiguationData":[TD([[makeQuery(id+"F2.imprint","INTERSECT",VERTEX,{"derivedFrom":[subQ0,sQuery(id+"F2.wireOp",EDGE,"E10.trimOffspring")]}),1.0]])],"derivedFrom":subQ0})])],"isStart":true});}
            var Q83;
            Q83=makeQuery(id+"F3.opExtrude","CAP_EDGE",EDGE,{"disambiguationData":[OSD([sQuery(id+"F2.wireOp",EDGE,"E13.19.2")])],"isStart":true});
            var Q84;
            Q84=makeQuery(id+"F3.opExtrude","CAP_EDGE",EDGE,{"disambiguationData":[OSD([sQuery(id+"F2.wireOp",EDGE,"E13.19.0")])],"isStart":true});
            var Q85;
            {var subQ0=sQuery(id+"F2.wireOp",EDGE,"E0");Q85=makeQuery(id+"F3.opExtrude","CAP_EDGE",EDGE,{"disambiguationData":[OSD([subQ0]),TDD([makeQuery(id+"F2.imprint","IMPRINT",EDGE,{"disambiguationData":[TD([[makeQuery(id+"F2.imprint","INTERSECT",VERTEX,{"derivedFrom":[subQ0,sQuery(id+"F2.wireOp",EDGE,"E13.18.2")]}),-1.0]])],"derivedFrom":subQ0})])],"isStart":true});}
            var Q86;
            Q86=makeQuery(id+"F3.opExtrude","CAP_EDGE",EDGE,{"disambiguationData":[OSD([sQuery(id+"F2.wireOp",EDGE,"E13.18.2")])],"isStart":true});
            var Q87;
            Q87=makeQuery(id+"F3.opExtrude","CAP_EDGE",EDGE,{"disambiguationData":[OSD([sQuery(id+"F2.wireOp",EDGE,"E13.18.0")])],"isStart":true});
            var Q88;
            {var subQ0=sQuery(id+"F2.wireOp",EDGE,"E0");Q88=makeQuery(id+"F3.opExtrude","CAP_EDGE",EDGE,{"disambiguationData":[OSD([subQ0]),TDD([makeQuery(id+"F2.imprint","IMPRINT",EDGE,{"disambiguationData":[TD([[makeQuery(id+"F2.imprint","INTERSECT",VERTEX,{"derivedFrom":[subQ0,sQuery(id+"F2.wireOp",EDGE,"E13.17.2")]}),-1.0]])],"derivedFrom":subQ0})])],"isStart":true});}
            var Q89;
            Q89=makeQuery(id+"F3.opExtrude","CAP_EDGE",EDGE,{"disambiguationData":[OSD([sQuery(id+"F2.wireOp",EDGE,"E13.17.2")])],"isStart":true});
            var Q90;
            Q90=makeQuery(id+"F3.opExtrude","CAP_EDGE",EDGE,{"disambiguationData":[OSD([sQuery(id+"F2.wireOp",EDGE,"E13.17.0")])],"isStart":true});
            var Q91;
            {var subQ0=sQuery(id+"F2.wireOp",EDGE,"E0");Q91=makeQuery(id+"F3.opExtrude","CAP_EDGE",EDGE,{"disambiguationData":[OSD([subQ0]),TDD([makeQuery(id+"F2.imprint","IMPRINT",EDGE,{"disambiguationData":[TD([[makeQuery(id+"F2.imprint","INTERSECT",VERTEX,{"derivedFrom":[subQ0,sQuery(id+"F2.wireOp",EDGE,"E13.16.2")]}),-1.0]])],"derivedFrom":subQ0})])],"isStart":true});}
            var Q92;
            Q92=makeQuery(id+"F3.opExtrude","CAP_EDGE",EDGE,{"disambiguationData":[OSD([sQuery(id+"F2.wireOp",EDGE,"E13.16.2")])],"isStart":true});
            var Q93;
            Q93=makeQuery(id+"F3.opExtrude","CAP_EDGE",EDGE,{"disambiguationData":[OSD([sQuery(id+"F2.wireOp",EDGE,"E13.16.0")])],"isStart":true});
            var Q94;
            {var subQ0=sQuery(id+"F2.wireOp",EDGE,"E0");Q94=makeQuery(id+"F3.opExtrude","CAP_EDGE",EDGE,{"disambiguationData":[OSD([subQ0]),TDD([makeQuery(id+"F2.imprint","IMPRINT",EDGE,{"disambiguationData":[TD([[makeQuery(id+"F2.imprint","INTERSECT",VERTEX,{"derivedFrom":[subQ0,sQuery(id+"F2.wireOp",EDGE,"E13.15.2")]}),-1.0]])],"derivedFrom":subQ0})])],"isStart":true});}
            var Q95;
            Q95=makeQuery(id+"F3.opExtrude","CAP_EDGE",EDGE,{"disambiguationData":[OSD([sQuery(id+"F2.wireOp",EDGE,"E13.15.2")])],"isStart":true});
            var Q96;
            Q96=makeQuery(id+"F3.opExtrude","CAP_EDGE",EDGE,{"disambiguationData":[OSD([sQuery(id+"F2.wireOp",EDGE,"E13.15.0")])],"isStart":true});
            var Q97;
            {var subQ0=sQuery(id+"F2.wireOp",EDGE,"E0");Q97=makeQuery(id+"F3.opExtrude","CAP_EDGE",EDGE,{"disambiguationData":[OSD([subQ0]),TDD([makeQuery(id+"F2.imprint","IMPRINT",EDGE,{"disambiguationData":[TD([[makeQuery(id+"F2.imprint","INTERSECT",VERTEX,{"derivedFrom":[subQ0,sQuery(id+"F2.wireOp",EDGE,"E13.14.2")]}),-1.0]])],"derivedFrom":subQ0})])],"isStart":true});}
            var Q98;
            Q98=makeQuery(id+"F3.opExtrude","CAP_EDGE",EDGE,{"disambiguationData":[OSD([sQuery(id+"F2.wireOp",EDGE,"E13.14.2")])],"isStart":true});
            var Q99;
            Q99=makeQuery(id+"F3.opExtrude","CAP_EDGE",EDGE,{"disambiguationData":[OSD([sQuery(id+"F2.wireOp",EDGE,"E13.14.0")])],"isStart":true});
            var Q100;
            {var subQ0=sQuery(id+"F2.wireOp",EDGE,"E0");Q100=makeQuery(id+"F3.opExtrude","CAP_EDGE",EDGE,{"disambiguationData":[OSD([subQ0]),TDD([makeQuery(id+"F2.imprint","IMPRINT",EDGE,{"disambiguationData":[TD([[makeQuery(id+"F2.imprint","INTERSECT",VERTEX,{"derivedFrom":[subQ0,sQuery(id+"F2.wireOp",EDGE,"E13.13.2")]}),-1.0]])],"derivedFrom":subQ0})])],"isStart":true});}
            var Q101;
            Q101=makeQuery(id+"F3.opExtrude","CAP_EDGE",EDGE,{"disambiguationData":[OSD([sQuery(id+"F2.wireOp",EDGE,"E13.13.2")])],"isStart":true});
            var Q102;
            Q102=makeQuery(id+"F3.opExtrude","CAP_EDGE",EDGE,{"disambiguationData":[OSD([sQuery(id+"F2.wireOp",EDGE,"E13.13.0")])],"isStart":true});
            var Q103;
            {var subQ0=sQuery(id+"F2.wireOp",EDGE,"E0");Q103=makeQuery(id+"F3.opExtrude","CAP_EDGE",EDGE,{"disambiguationData":[OSD([subQ0]),TDD([makeQuery(id+"F2.imprint","IMPRINT",EDGE,{"disambiguationData":[TD([[makeQuery(id+"F2.imprint","INTERSECT",VERTEX,{"derivedFrom":[subQ0,sQuery(id+"F2.wireOp",EDGE,"E13.12.2")]}),-1.0]])],"derivedFrom":subQ0})])],"isStart":true});}
            var Q104;
            Q104=makeQuery(id+"F3.opExtrude","CAP_EDGE",EDGE,{"disambiguationData":[OSD([sQuery(id+"F2.wireOp",EDGE,"E13.12.2")])],"isStart":true});
            var Q105;
            Q105=makeQuery(id+"F3.opExtrude","CAP_EDGE",EDGE,{"disambiguationData":[OSD([sQuery(id+"F2.wireOp",EDGE,"E13.12.0")])],"isStart":true});
            var Q106;
            {var subQ0=sQuery(id+"F2.wireOp",EDGE,"E0");Q106=makeQuery(id+"F3.opExtrude","CAP_EDGE",EDGE,{"disambiguationData":[OSD([subQ0]),TDD([makeQuery(id+"F2.imprint","IMPRINT",EDGE,{"disambiguationData":[TD([[makeQuery(id+"F2.imprint","INTERSECT",VERTEX,{"derivedFrom":[subQ0,sQuery(id+"F2.wireOp",EDGE,"E13.11.2")]}),-1.0]])],"derivedFrom":subQ0})])],"isStart":true});}
            var Q107;
            Q107=makeQuery(id+"F3.opExtrude","CAP_EDGE",EDGE,{"disambiguationData":[OSD([sQuery(id+"F2.wireOp",EDGE,"E13.11.2")])],"isStart":true});
            var Q108;
            Q108=makeQuery(id+"F3.opExtrude","CAP_EDGE",EDGE,{"disambiguationData":[OSD([sQuery(id+"F2.wireOp",EDGE,"E13.11.0")])],"isStart":true});
            var Q109;
            {var subQ0=sQuery(id+"F2.wireOp",EDGE,"E0");Q109=makeQuery(id+"F3.opExtrude","CAP_EDGE",EDGE,{"disambiguationData":[OSD([subQ0]),TDD([makeQuery(id+"F2.imprint","IMPRINT",EDGE,{"disambiguationData":[TD([[makeQuery(id+"F2.imprint","INTERSECT",VERTEX,{"derivedFrom":[subQ0,sQuery(id+"F2.wireOp",EDGE,"E13.10.2")]}),-1.0]])],"derivedFrom":subQ0})])],"isStart":true});}
            var Q110;
            Q110=makeQuery(id+"F3.opExtrude","CAP_EDGE",EDGE,{"disambiguationData":[OSD([sQuery(id+"F2.wireOp",EDGE,"E13.10.2")])],"isStart":true});
            var Q111;
            Q111=makeQuery(id+"F3.opExtrude","CAP_EDGE",EDGE,{"disambiguationData":[OSD([sQuery(id+"F2.wireOp",EDGE,"E13.10.0")])],"isStart":true});
            var Q112;
            {var subQ0=sQuery(id+"F2.wireOp",EDGE,"E0");Q112=makeQuery(id+"F3.opExtrude","CAP_EDGE",EDGE,{"disambiguationData":[OSD([subQ0]),TDD([makeQuery(id+"F2.imprint","IMPRINT",EDGE,{"disambiguationData":[TD([[makeQuery(id+"F2.imprint","INTERSECT",VERTEX,{"derivedFrom":[subQ0,sQuery(id+"F2.wireOp",EDGE,"E13.9.2")]}),-1.0]])],"derivedFrom":subQ0})])],"isStart":true});}
            var Q113;
            Q113=makeQuery(id+"F3.opExtrude","CAP_EDGE",EDGE,{"disambiguationData":[OSD([sQuery(id+"F2.wireOp",EDGE,"E13.9.2")])],"isStart":true});
            var Q114;
            Q114=makeQuery(id+"F3.opExtrude","CAP_EDGE",EDGE,{"disambiguationData":[OSD([sQuery(id+"F2.wireOp",EDGE,"E13.9.0")])],"isStart":true});
            var Q115;
            {var subQ0=sQuery(id+"F2.wireOp",EDGE,"E0");Q115=makeQuery(id+"F3.opExtrude","CAP_EDGE",EDGE,{"disambiguationData":[OSD([subQ0]),TDD([makeQuery(id+"F2.imprint","IMPRINT",EDGE,{"disambiguationData":[TD([[makeQuery(id+"F2.imprint","INTERSECT",VERTEX,{"derivedFrom":[subQ0,sQuery(id+"F2.wireOp",EDGE,"E13.8.2")]}),-1.0]])],"derivedFrom":subQ0})])],"isStart":true});}
            var Q116;
            Q116=makeQuery(id+"F3.opExtrude","CAP_EDGE",EDGE,{"disambiguationData":[OSD([sQuery(id+"F2.wireOp",EDGE,"E13.8.2")])],"isStart":true});
            fillet(context, id + "F4", {"entities" : qUnion([Q0, Q1, Q2, Q3, Q4, Q5, Q6, Q7, Q8, Q9, Q10, Q11, Q12, Q13, Q14, Q15, Q16, Q17, Q18, Q19, Q20, Q21, Q22, Q23, Q24, Q25, Q26, Q27, Q28, Q29, Q30, Q31, Q32, Q33, Q34, Q35, Q36, Q37, Q38, Q39, Q40, Q41, Q42, Q43, Q44, Q45, Q46, Q47, Q48, Q49, Q50, Q51, Q52, Q53, Q54, Q55, Q56, Q57, Q58, Q59, Q60, Q61, Q62, Q63, Q64, Q65, Q66, Q67, Q68, Q69, Q70, Q71, Q72, Q73, Q74, Q75, Q76, Q77, Q78, Q79, Q80, Q81, Q82, Q83, Q84, Q85, Q86, Q87, Q88, Q89, Q90, Q91, Q92, Q93, Q94, Q95, Q96, Q97, Q98, Q99, Q100, Q101, Q102, Q103, Q104, Q105, Q106, Q107, Q108, Q109, Q110, Q111, Q112, Q113, Q114, Q115, Q116]), "radius" : (getVariable(context, 'TeethFillet')) * mm, "tangentPropagation" : true, "allowEdgeOverflow" : false});
        }
    });
